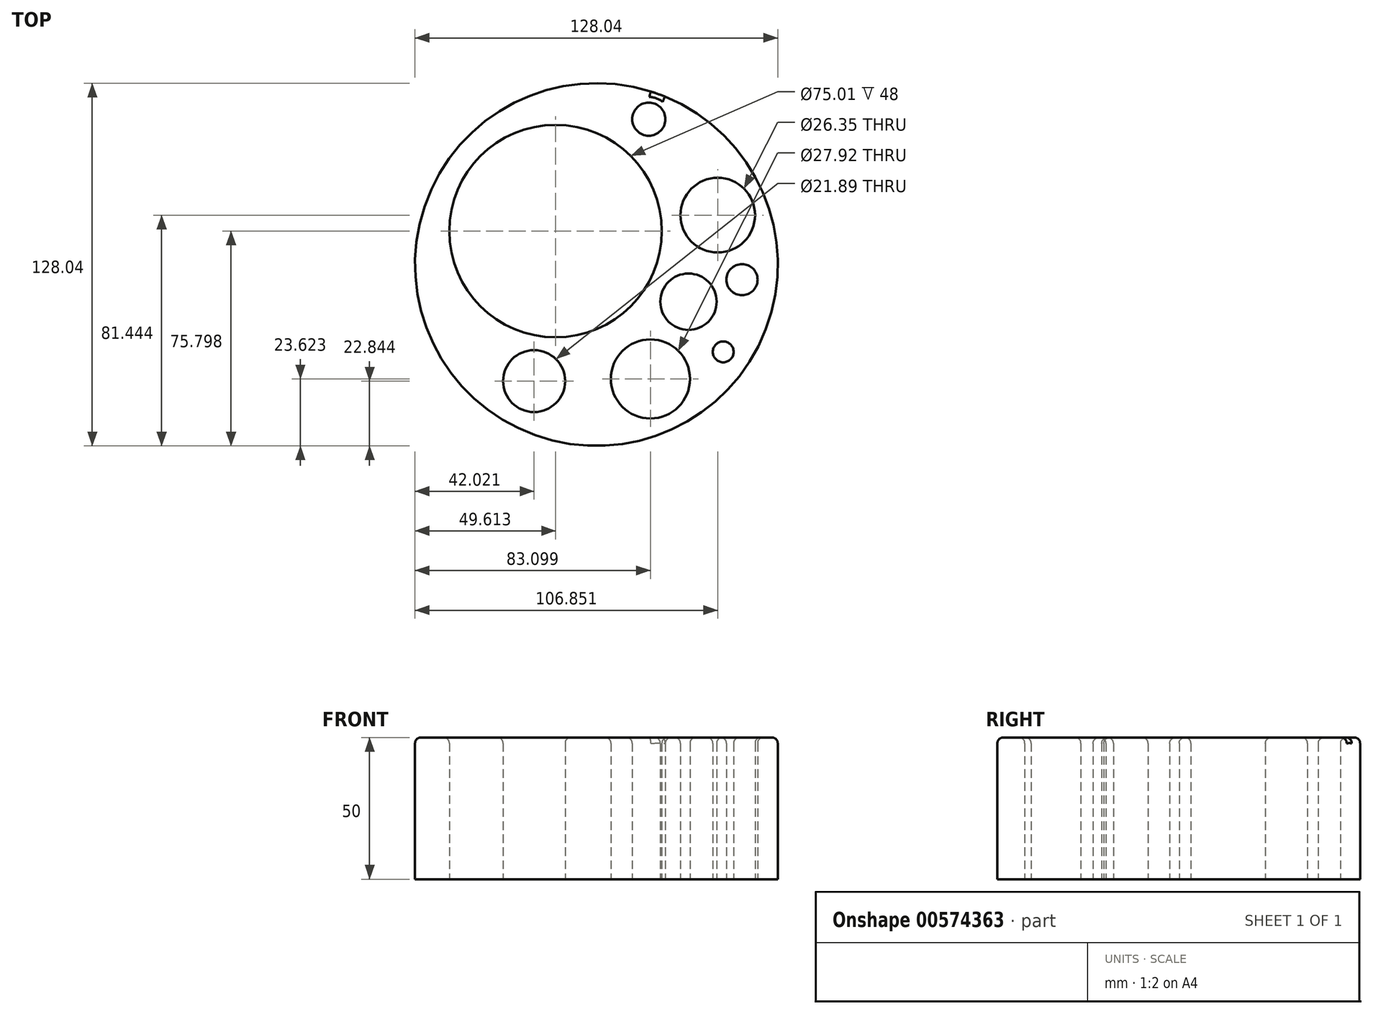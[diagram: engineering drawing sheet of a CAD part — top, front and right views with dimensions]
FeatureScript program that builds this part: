
annotation { "Feature Type Name" : "Feature", "Feature Type Description" : "" }
export const myFeature = defineFeature(function(context is Context, id is Id, definition is map)
    precondition{}
    {
        {
            var Q0;
            Q0=qCreatedBy(makeId("Top.planeOp"),FACE);
            var sketch = newSketch(context, id + "F0", { "sketchPlane" : qUnion([Q0])});
            skCircle(sketch, "E0", {"center": v(0, 0) * mm, "radius": 64.02 * mm});
            skCircle(sketch, "E1", {"center": v(-14.4, 11.78) * mm, "radius": 37.5 * mm});
            skCircle(sketch, "E2", {"center": v(42.83, 17.42) * mm, "radius": 13.18 * mm});
            skCircle(sketch, "E3", {"center": v(19.08, -40.4) * mm, "radius": 13.96 * mm});
            skCircle(sketch, "E4", {"center": v(32.51, -13.14) * mm, "radius": 9.94 * mm});
            skCircle(sketch, "E5", {"center": v(51.4, -5.35) * mm, "radius": 5.5 * mm});
            skCircle(sketch, "E6", {"center": v(44.78, -30.86) * mm, "radius": 3.67 * mm});
            skCircle(sketch, "E7", {"center": v(18.5, 51.3) * mm, "radius": 5.86 * mm});
            skCircle(sketch, "E8", {"center": v(-22, -41.18) * mm, "radius": 10.95 * mm});
            skSolve(sketch);
        }
        {
            var Q0;
            Q0=makeQuery(id+"F0.imprint","IMPRINT",FACE,{"disambiguationData":[TD([[makeQuery(id+"F0.imprint","IMPRINT",EDGE,{"derivedFrom":sQuery(id+"F0.wireOp",EDGE,"E0")}),1.0]])]});
            extrude(context, id + "F1", {"entities" : qUnion([Q0]), "depth" : 25 * mm, "offsetDistance" : 25 * mm});
        }
        {
            var Q0;
            Q0=makeQuery(id+"F1.opExtrude","CAP_FACE",FACE,{"disambiguationData":[OSD([sQuery(id+"F0.wireOp",EDGE,"E0"),sQuery(id+"F0.wireOp",EDGE,"E1"),sQuery(id+"F0.wireOp",EDGE,"E2"),sQuery(id+"F0.wireOp",EDGE,"E3"),sQuery(id+"F0.wireOp",EDGE,"E4"),sQuery(id+"F0.wireOp",EDGE,"E5"),sQuery(id+"F0.wireOp",EDGE,"E6"),sQuery(id+"F0.wireOp",EDGE,"E7"),sQuery(id+"F0.wireOp",EDGE,"E8")])],"isStart":false});
            extrude(context, id + "F2", {"entities" : qUnion([Q0]), "operationType" : NewBodyOperationType.ADD, "depth" : 25 * mm, "offsetDistance" : 25 * mm});
        }
        {
            var Q0;
            Q0=makeQuery(id+"F2.opExtrude","CAP_EDGE",EDGE,{"disambiguationData":[OSD([sQuery(id+"F0.wireOp",EDGE,"E3")])],"isStart":false});
            var Q1;
            Q1=makeQuery(id+"F2.opExtrude","CAP_EDGE",EDGE,{"disambiguationData":[OSD([sQuery(id+"F0.wireOp",EDGE,"E1")])],"isStart":false});
            var Q2;
            Q2=makeQuery(id+"F2.opExtrude","CAP_EDGE",EDGE,{"disambiguationData":[OSD([sQuery(id+"F0.wireOp",EDGE,"E5")])],"isStart":false});
            var Q3;
            Q3=makeQuery(id+"F2.opExtrude","CAP_EDGE",EDGE,{"disambiguationData":[OSD([sQuery(id+"F0.wireOp",EDGE,"E4")])],"isStart":false});
            var Q4;
            Q4=makeQuery(id+"F2.opExtrude","CAP_EDGE",EDGE,{"disambiguationData":[OSD([sQuery(id+"F0.wireOp",EDGE,"E7")])],"isStart":false});
            var Q5;
            Q5=makeQuery(id+"F2.opExtrude","CAP_EDGE",EDGE,{"disambiguationData":[OSD([sQuery(id+"F0.wireOp",EDGE,"E6")])],"isStart":false});
            var Q6;
            Q6=makeQuery(id+"F2.opExtrude","CAP_EDGE",EDGE,{"disambiguationData":[OSD([sQuery(id+"F0.wireOp",EDGE,"E8")])],"isStart":false});
            var Q7;
            Q7=makeQuery(id+"F2.opExtrude","CAP_EDGE",EDGE,{"disambiguationData":[OSD([sQuery(id+"F0.wireOp",EDGE,"E2")])],"isStart":false});
            fillet(context, id + "F3", {"entities" : qUnion([Q0, Q1, Q2, Q3, Q4, Q5, Q6, Q7]), "radius" : 2 * mm, "tangentPropagation" : true, "allowEdgeOverflow" : false});
        }
        {
            var Q0;
            Q0=makeQuery(id+"F2.opExtrude","CAP_EDGE",EDGE,{"disambiguationData":[OSD([sQuery(id+"F0.wireOp",EDGE,"E0")])],"isStart":false});
            fillet(context, id + "F4", {"entities" : qUnion([Q0]), "radius" : 2 * mm, "tangentPropagation" : true, "allowEdgeOverflow" : false});
        }
        {
            var Q0;
            Q0=makeQuery(id+"F2.opExtrude","CAP_FACE",FACE,{"disambiguationData":[OSD([sQuery(id+"F0.wireOp",EDGE,"E0"),sQuery(id+"F0.wireOp",EDGE,"E1"),sQuery(id+"F0.wireOp",EDGE,"E2"),sQuery(id+"F0.wireOp",EDGE,"E3"),sQuery(id+"F0.wireOp",EDGE,"E4"),sQuery(id+"F0.wireOp",EDGE,"E5"),sQuery(id+"F0.wireOp",EDGE,"E6"),sQuery(id+"F0.wireOp",EDGE,"E7"),sQuery(id+"F0.wireOp",EDGE,"E8")])],"isStart":false});
            extrude(context, id + "F5", {"entities" : qUnion([Q0]), "operationType" : NewBodyOperationType.REMOVE, "depth" : 100 * mm, "offsetDistance" : 25 * mm});
        }
    });
